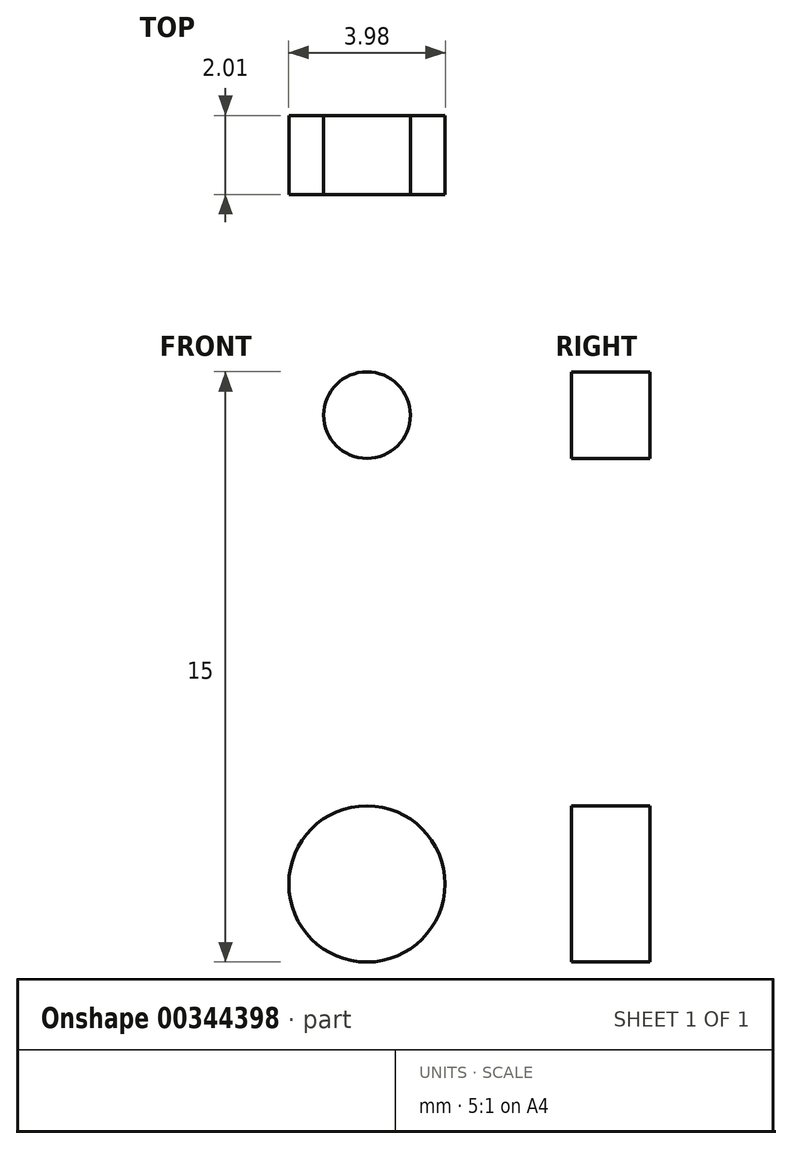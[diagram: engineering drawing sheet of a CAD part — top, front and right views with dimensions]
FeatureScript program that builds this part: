
annotation { "Feature Type Name" : "Feature", "Feature Type Description" : "" }
export const myFeature = defineFeature(function(context is Context, id is Id, definition is map)
    precondition{}
    {
        {
            var Q0;
            Q0=qCreatedBy(makeId("Right.planeOp"),FACE);
            var sketch = newSketch(context, id + "F0", { "sketchPlane" : qUnion([Q0])});
            skLineSegment(sketch, "E0.bottom", {"start": v(24.6, 11.12) * mm, "end": v(-24.6, 11.12) * mm});
            skLineSegment(sketch, "E0.top", {"start": v(24.6, -11.12) * mm, "end": v(-24.6, -11.12) * mm});
            skLineSegment(sketch, "E0.left", {"start": v(24.6, 11.12) * mm, "end": v(24.6, -11.12) * mm});
            skLineSegment(sketch, "E0.right", {"start": v(-24.6, 11.12) * mm, "end": v(-24.6, -11.12) * mm});
            skPoint(sketch, "E0.middle", {"position": v(0, 0) * mm});
            skLineSegment(sketch, "E1.0", {"start": v(-22.6, 11.12) * mm, "end": v(-22.6, -9.12) * mm});
            skLineSegment(sketch, "E1.1", {"start": v(24.6, -9.12) * mm, "end": v(-22.6, -9.12) * mm});
            skSolve(sketch);
        }
        {
            var Q0;
            {var subQ2=sQuery(id+"F0.wireOp",EDGE,"E0.top");Q0=makeQuery(id+"F0.imprint","IMPRINT",FACE,{"disambiguationData":[TD([[makeQuery(id+"F0.imprint","IMPRINT",EDGE,{"derivedFrom":subQ2}),-1.0]])]});}
            extrude(context, id + "F1", {"entities" : qUnion([Q0]), "endBound" : BoundingType.SYMMETRIC, "depth" : 25.4 * mm});
        }
        {
            var Q0;
            Q0=makeQuery(id+"F1.opExtrude","SWEPT_FACE",FACE,{"disambiguationData":[OSD([sQuery(id+"F0.wireOp",EDGE,"E1.1")])]});
            var sketch = newSketch(context, id + "F2", { "sketchPlane" : qUnion([Q0])});
            skCircle(sketch, "E2", {"center": v(-8.73, 3.18) * mm, "radius": 1.99 * mm});
            skCircle(sketch, "E3.MirrorC", {"center": v(8.73, 3.18) * mm, "radius": 1.99 * mm});
            skLineSegment(sketch, "E4", {"start": v(-8.73, 34.25) * mm, "end": v(-8.73, -43.96) * mm, "construction": true});
            skSolve(sketch);
        }
        {
            var Q0;
            Q0=makeQuery(id+"F1.opExtrude","SWEPT_FACE",FACE,{"disambiguationData":[OSD([sQuery(id+"F0.wireOp",EDGE,"E0.right")])]});
            var sketch = newSketch(context, id + "F3", { "sketchPlane" : qUnion([Q0])});
            skPoint(sketch, "E5.0", {"position": v(-8.73, -9.12) * mm});
            skLineSegment(sketch, "E6", {"start": v(-8.73, -16.36) * mm, "end": v(-8.73, 27.84) * mm, "construction": true});
            skCircle(sketch, "E7", {"center": v(-8.73, -4.76) * mm, "radius": 1.99 * mm});
            skCircle(sketch, "E8", {"center": v(-8.73, 7.15) * mm, "radius": 1.1 * mm});
            skCircle(sketch, "E9.MirrorC", {"center": v(8.73, 7.15) * mm, "radius": 1.1 * mm});
            skCircle(sketch, "E10.MirrorC", {"center": v(8.73, -4.76) * mm, "radius": 1.99 * mm});
            skSolve(sketch);
        }
        {
            var Q0;
            Q0=makeQuery(id+"F3.imprint","IMPRINT",FACE,{"disambiguationData":[TD([[makeQuery(id+"F3.imprint","IMPRINT",EDGE,{"derivedFrom":sQuery(id+"F3.wireOp",EDGE,"E10.MirrorC")}),-1.0]])]});
            var Q1;
            Q1=makeQuery(id+"F3.imprint","IMPRINT",FACE,{"disambiguationData":[TD([[makeQuery(id+"F3.imprint","IMPRINT",EDGE,{"derivedFrom":sQuery(id+"F3.wireOp",EDGE,"E9.MirrorC")}),-1.0]])]});
            var Q2;
            Q2=makeQuery(id+"F3.imprint","IMPRINT",FACE,{"disambiguationData":[TD([[makeQuery(id+"F3.imprint","IMPRINT",EDGE,{"derivedFrom":sQuery(id+"F3.wireOp",EDGE,"E7")}),1.0]])]});
            var Q3;
            Q3=makeQuery(id+"F3.imprint","IMPRINT",FACE,{"disambiguationData":[TD([[makeQuery(id+"F3.imprint","IMPRINT",EDGE,{"derivedFrom":sQuery(id+"F3.wireOp",EDGE,"E8")}),1.0]])]});
            extrude(context, id + "F4", {"entities" : qUnion([Q0, Q1, Q2, Q3]), "operationType" : NewBodyOperationType.REMOVE, "endBound" : BoundingType.THROUGH_ALL, "oppositeDirection" : true, "depth" : 25 * mm});
        }
        {
            var Q0;
            Q0=makeQuery(id+"F2.imprint","IMPRINT",FACE,{"disambiguationData":[TD([[makeQuery(id+"F2.imprint","IMPRINT",EDGE,{"derivedFrom":sQuery(id+"F2.wireOp",EDGE,"E2")}),1.0]])]});
            var Q1;
            Q1=makeQuery(id+"F2.imprint","IMPRINT",FACE,{"disambiguationData":[TD([[makeQuery(id+"F2.imprint","IMPRINT",EDGE,{"derivedFrom":sQuery(id+"F2.wireOp",EDGE,"E3.MirrorC")}),-1.0]])]});
            extrude(context, id + "F5", {"entities" : qUnion([Q0, Q1]), "operationType" : NewBodyOperationType.REMOVE, "endBound" : BoundingType.THROUGH_ALL, "oppositeDirection" : true, "depth" : 25 * mm});
        }
    });
